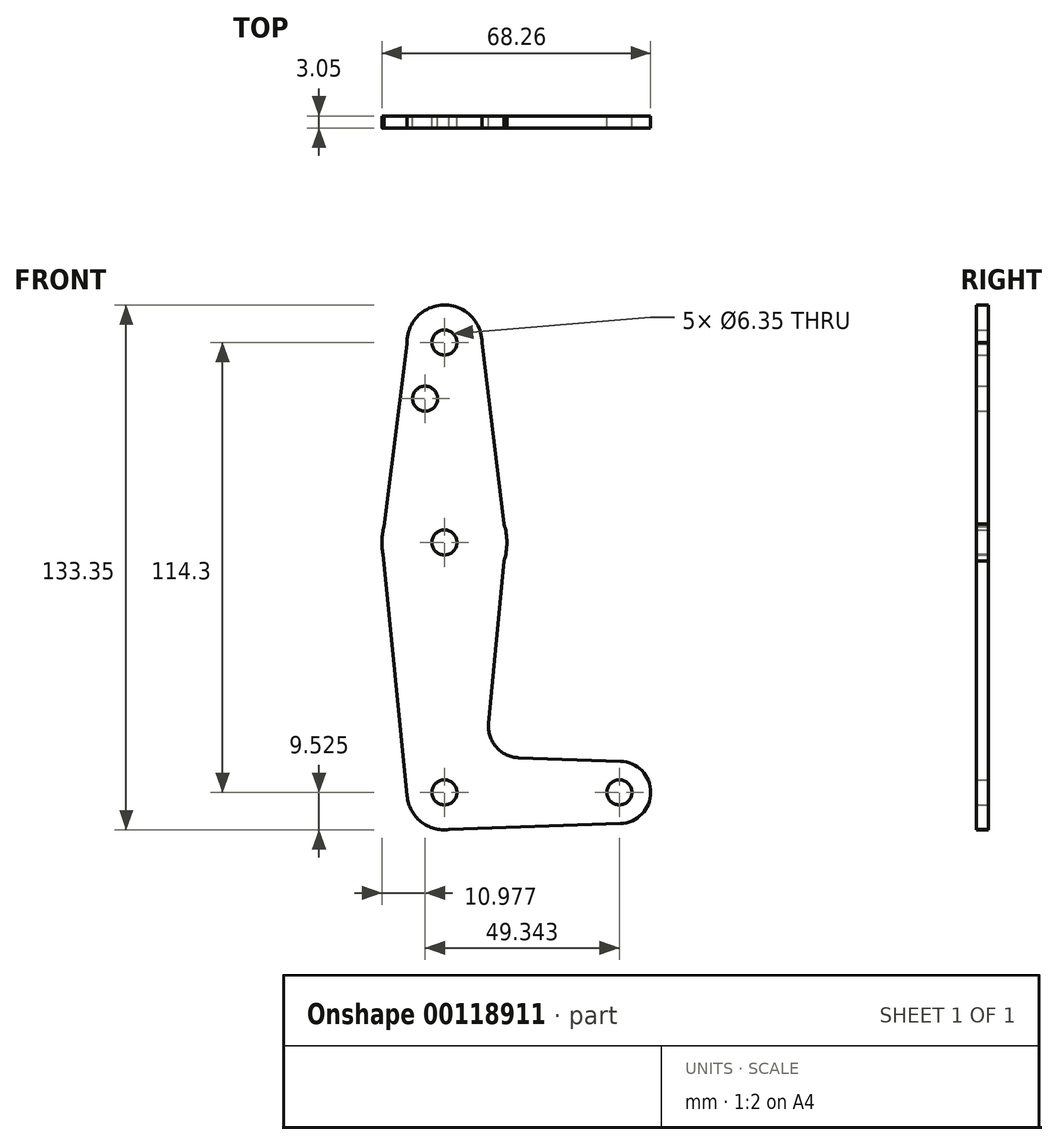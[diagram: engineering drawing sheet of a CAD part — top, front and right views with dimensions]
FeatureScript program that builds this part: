
annotation { "Feature Type Name" : "Feature", "Feature Type Description" : "" }
export const myFeature = defineFeature(function(context is Context, id is Id, definition is map)
    precondition{}
    {
        {
            var Q0;
            Q0=qCreatedBy(makeId("Front.planeOp"),FACE);
            var sketch = newSketch(context, id + "F0", { "sketchPlane" : qUnion([Q0])});
            skLineSegment(sketch, "E0", {"start": v(-28.93, 89.58) * mm, "end": v(-28.93, -24.72) * mm});
            skLineSegment(sketch, "E1", {"start": v(-28.93, -24.72) * mm, "end": v(15.52, -24.72) * mm});
            skCircle(sketch, "E2", {"center": v(-28.93, 89.58) * mm, "radius": 9.53 * mm});
            skCircle(sketch, "E3", {"center": v(-28.93, -24.72) * mm, "radius": 9.53 * mm});
            skCircle(sketch, "E4", {"center": v(15.52, -24.72) * mm, "radius": 7.94 * mm});
            skCircle(sketch, "E5", {"center": v(-28.93, 38.78) * mm, "radius": 15.88 * mm});
            skLineSegment(sketch, "E6", {"start": v(-19.4, 89.62) * mm, "end": v(-13.08, 37.9) * mm});
            skLineSegment(sketch, "E7", {"start": v(-13.77, 34.07) * mm, "end": v(-17.7, -7.2) * mm});
            skLineSegment(sketch, "E8", {"start": v(-38.45, 89.2) * mm, "end": v(-44.8, 38.62) * mm});
            skLineSegment(sketch, "E9", {"start": v(-44.8, 38.62) * mm, "end": v(-38.4, -25.66) * mm});
            skLineSegment(sketch, "E10", {"start": v(-10.05, -15.9) * mm, "end": v(15.79, -16.78) * mm});
            skLineSegment(sketch, "E11", {"start": v(-27.75, -34.17) * mm, "end": v(15.8, -32.65) * mm});
            skCircle(sketch, "E12", {"center": v(-28.93, 89.58) * mm, "radius": 3.18 * mm});
            skCircle(sketch, "E13", {"center": v(-33.82, 75.31) * mm, "radius": 3.18 * mm});
            skCircle(sketch, "E14", {"center": v(-28.93, 38.78) * mm, "radius": 3.18 * mm});
            skCircle(sketch, "E15", {"center": v(-28.93, -24.72) * mm, "radius": 3.18 * mm});
            skCircle(sketch, "E16", {"center": v(15.52, -24.72) * mm, "radius": 3.18 * mm});
            skArc(sketch, "E17.filletArc", {"start": v(-17.7, -7.2) * mm, "mid": v(-15.75, -13.2) * mm, "end": v(-10.05, -15.9) * mm});
            skSolve(sketch);
        }
        {
            var Q0;
            Q0 = qSketchRegion(id + "F0", true);
            var Q1;
            {var subQ0=sQuery(id+"F0.wireOp",EDGE,"E3");var subQ1=sQuery(id+"F0.wireOp",EDGE,"E0");var subQ2=makeQuery(id+"F0.imprint","INTERSECT",VERTEX,{"derivedFrom":[subQ1,subQ0]});Q1=makeQuery(id+"F0.imprint","IMPRINT",FACE,{"disambiguationData":[TD([[makeQuery(id+"F0.imprint","IMPRINT",EDGE,{"disambiguationData":[TD([[subQ2,-1.0]])],"derivedFrom":subQ1}),1.0]])]});}
            extrude(context, id + "F1", {"entities" : qUnion([Q0, Q1]), "depth" : 3.05 * mm});
        }
    });
